# Revit family: Shower_Head-GROHE-New_Tempesta_Cosmopolitan_100-26366001
name_source: partatom
category: Plumbing Fixtures
revit_build: Autodesk Revit 2014 (Build: 20130308_1515(x64)
units: mm (PartAtom-declared; Revit-internal decimal feet)

## types (1)
- 26366001
    Assembly Code = D2010700
    CW Connection = Yes
    CWFU = 3
    CalGreen Compliant = Yes
    Cold Water Connection Diameter = 1/2"
    Cold Water Connection Radius = 1/4"
    Default Elevation = 0"
    Description = New Tempesta Cosmopolitan 100 Shower Head 1 Spray
    Finish = Metal-Grohe-001-Chrome
    Flow Rate = 1.75 gpm (6.6 L/min)
    HW Connection = Yes
    HWFU = 3
    Height = 3 3/8"
    Hot Water Connection Diameter = 1"
    Hot Water Connection Radius = 1/4"
    Manufacturer = GROHE
    Material = Metal-Grohe-001-Chrome
    Model = 26366001
    Price = Prices may vary. Please consult Manufacturer Representative for most up-to-date price list.
    Product Page URL = https://www.grohe.us
    Tempered Water Connection Diameter = 1/2"
    Tempered Water Connection Radius = 1/4"
    URL = http://www.grohe.com
    Vent Connection = No
    WFU = 4
    Warranty Documentation Link = https://cdn.cloud.grohe.com
    Waste Connection = No
    Width = 3 15/16"
    cUPC Compliant = Yes

## geometry (parser evidence)
native form markers: Sweep x1
no freeform markers — native parametric forms only
